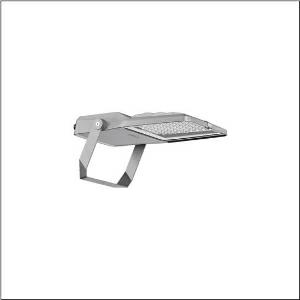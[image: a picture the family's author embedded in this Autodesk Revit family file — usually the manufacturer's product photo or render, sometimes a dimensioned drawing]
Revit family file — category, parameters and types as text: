
# Revit family: floodlight_fl_21_iq_mini___pl64_5xa7772c5e1a_f6c6
name_source: partatom
category: Lighting Fixtures
units: mm (PartAtom-declared; Revit-internal decimal feet)

## family parameters
Cut with Voids When Loaded = No
Host = Face
Light Source = No
Part Type = Normal
Room Calculation Point = No
Round Connector Dimension = Use Diameter
Shared = No

## types (1)
- --- (1 x LED, 11000 lm, 87.2 W, 4000K)
    Apparent Load = 87 VA
    CIE Flux Codes = 28 80 98 100 100
    Color Rendering = 80
    Color Temperature = 4000K
    Default Elevation = 1800 mm
    Description = Floodlight FL 21 iQ mini, floodlight, primary light control with lens, of PMMA, primary optical cover: protective disc, of toughened safety glass, transparent, light distribution: PL64, light emission: direct distribution, installation type: surface-mounted, LED, High Power LED, rated luminous flux: 11.000lm, luminous efficacy: 126lm/W, light colour: 840, colour temperature: 4000K, control gear: iQ Street-Remote/DALI, control: Street-Remote, Auto-Match, Temp-Guard, Night-Set, Smart-Wire, Desk-Remote (wireless, voltage-free reading and setting of iQ features in the workshop via application-optimized NFC function/RFID function), optimised constant luminous flux control (CLO 2.0), with terminal, 6-pole, mains connection: 220..240V, AC, 50/60Hz, start of lifetime: 87W, end of service life: 92W, reduction: 40W, luminaire housing, of diecast aluminium, powder-coated, Siteco® metallic grey (DB 702S), corrosivity category C5 mid according to DIN EN ISO 12944, suitable for swimming pools, chlorine-resistant, sealing non-destructively replaceable, mounting bracket, of steel, galvanised, powder-coated, Siteco® metallic grey (DB 702S), protection rating (complete): IP66, insulation class (complete): insulation class II (safety insulation), certification: CE, ENEC, VDE, protection symbol: D, impact resistance: IK08, permissible operating ambient temperature: -40..+40°C, permissible operating ambient temperature for outdoor applications: -40..+50°C, standard: DIN EN 12944, LABS conformity tested according to VDMA 24364:2018-05, packaging unit: 1 piece

Light Distribution: PL64
    Height = 70 mm
    Lamp = 1 x LED
    Lamp Light Flux = 11000 lm
    Lamp Power = 87.2 W
    Lamp count = 1
    Length = 485 mm
    Luminous efficacy = 126 lm/W
    Manufacturer = Siteco
    ModVariant = No
    Model = 5XA7772C5E1A
    Number of Poles = 1
    OnlyDefault = Yes
    Power Factor = 1
    Product Name = Floodlight FL 21 iQ mini | PL64
    Product group = floodlight | pylon annexe
    ProductGroupID = 6200
    Protection Class = Protection class II
    Protection Degree = IP 66
    RLX_Detail_Level = 1
    RLX_Emergency_Light_Flux = 0 lm
    RLX_Emergency_Type = 0
    RLX_Emergency_Type_DB = No
    RlxData = <blob elided: 96365 chars, md5=1b5bb086>
    Socket = socket
    Standby Power = 0 W
    System Light Flux = 11000 lm
    System Power = 87 W
    Type Comments = factory setting: luminous flux: 100 % | dim-lin: 254 | 456 mA
    Type Image = l_1006845.jpg
    URL = http://relux.com
    VarID = @adj_166182
    Voltage = 0 V
    Weight = 0.00 kg
    Width = 337 mm

## geometry (parser evidence)
native form markers: Blend x4, Sweep x15
no freeform markers — native parametric forms only
